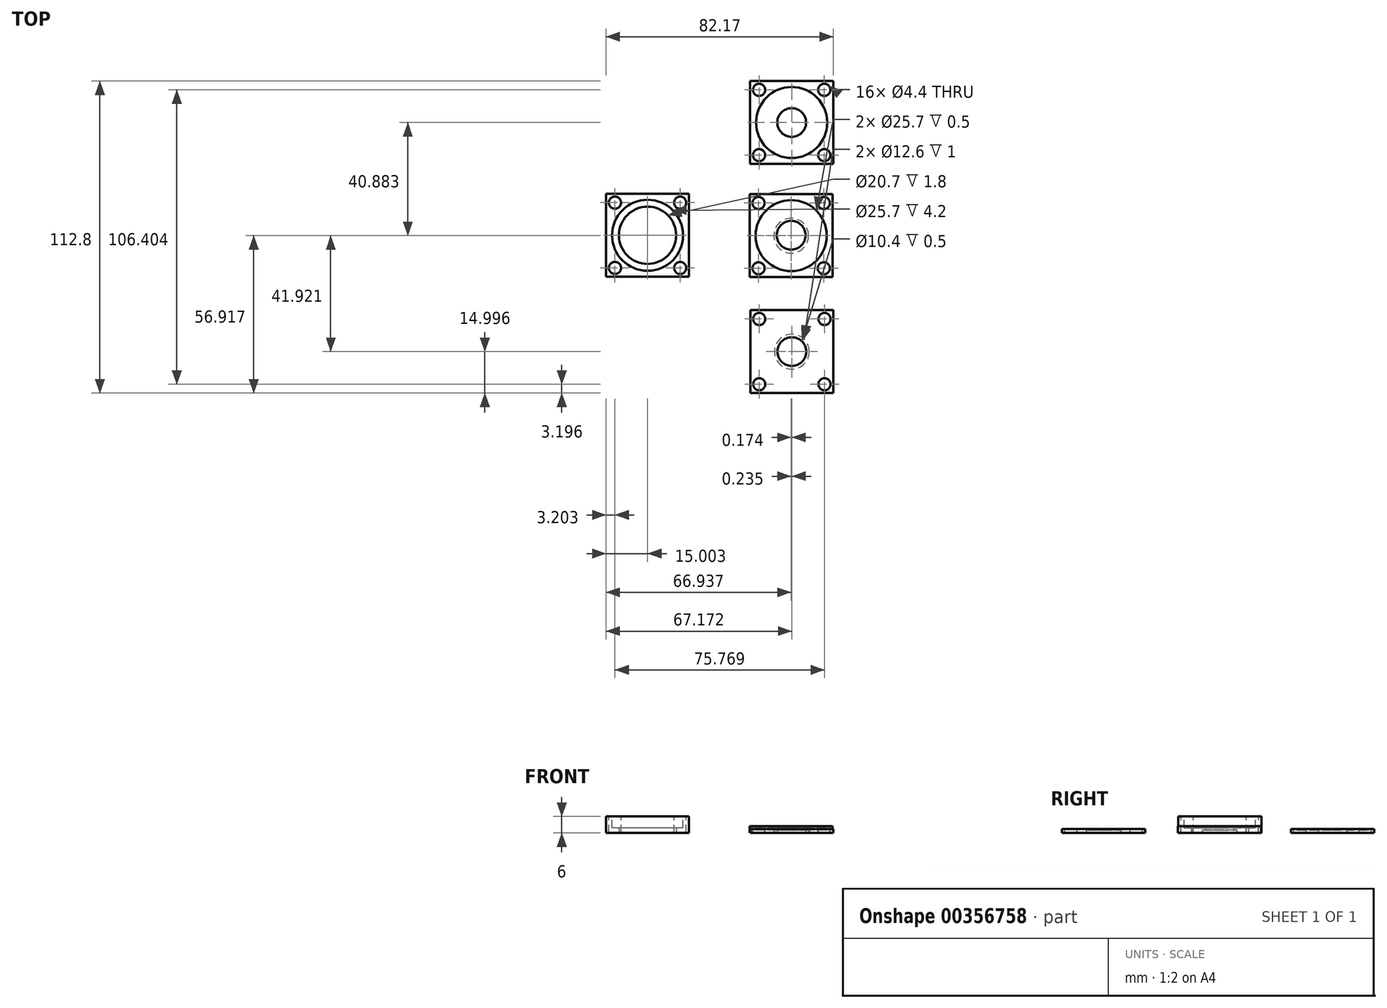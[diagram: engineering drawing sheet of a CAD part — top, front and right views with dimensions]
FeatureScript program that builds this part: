
annotation { "Feature Type Name" : "Feature", "Feature Type Description" : "" }
export const myFeature = defineFeature(function(context is Context, id is Id, definition is map)
    precondition{}
    {
        {
            var Q0;
            Q0=qCreatedBy(makeId("Top.planeOp"),FACE);
            var sketch = newSketch(context, id + "F0", { "sketchPlane" : qUnion([Q0])});
            skLineSegment(sketch, "E0.bottom", {"start": v(-9.76, 15) * mm, "end": v(-39.76, 15) * mm});
            skLineSegment(sketch, "E0.top", {"start": v(-9.76, -15) * mm, "end": v(-39.76, -15) * mm});
            skLineSegment(sketch, "E0.left", {"start": v(-9.76, 15) * mm, "end": v(-9.76, -15) * mm});
            skLineSegment(sketch, "E0.right", {"start": v(-39.76, 15) * mm, "end": v(-39.76, -15) * mm});
            skPoint(sketch, "E0.middle", {"position": v(-24.76, 0) * mm});
            skCircle(sketch, "E1", {"center": v(-24.76, 0) * mm, "radius": 10.35 * mm});
            skSolve(sketch);
        }
        {
            var Q0;
            Q0=makeQuery(id+"F0.imprint","IMPRINT",FACE,{"disambiguationData":[TD([[makeQuery(id+"F0.imprint","IMPRINT",EDGE,{"derivedFrom":sQuery(id+"F0.wireOp",EDGE,"E0.bottom")}),1.0]])]});
            extrude(context, id + "F1", {"entities" : qUnion([Q0]), "depth" : 6 * mm});
        }
        {
            var Q0;
            Q0=makeQuery(id+"F1.opExtrude","CAP_FACE",FACE,{"disambiguationData":[OSD([sQuery(id+"F0.wireOp",EDGE,"E0.bottom"),sQuery(id+"F0.wireOp",EDGE,"E0.top"),sQuery(id+"F0.wireOp",EDGE,"E0.left"),sQuery(id+"F0.wireOp",EDGE,"E0.right"),sQuery(id+"F0.wireOp",EDGE,"E1")])],"isStart":false});
            var sketch = newSketch(context, id + "F2", { "sketchPlane" : qUnion([Q0])});
            skLineSegment(sketch, "E2", {"start": v(-24.76, 15) * mm, "end": v(-24.76, -15) * mm, "construction": true});
            skLineSegment(sketch, "E3", {"start": v(-39.76, 0) * mm, "end": v(-9.76, 0) * mm, "construction": true});
            skCircle(sketch, "E4", {"center": v(-24.76, 0) * mm, "radius": 12.85 * mm});
            skSolve(sketch);
        }
        {
            var Q0;
            Q0=makeQuery(id+"F2.imprint","IMPRINT",FACE,{"disambiguationData":[TD([[makeQuery(id+"F2.imprint","IMPRINT",EDGE,{"derivedFrom":sQuery(id+"F2.wireOp",EDGE,"E4")}),1.0]])]});
            extrude(context, id + "F3", {"entities" : qUnion([Q0]), "operationType" : NewBodyOperationType.REMOVE, "oppositeDirection" : true, "depth" : 4.2 * mm});
        }
        {
            var Q0;
            Q0=makeQuery(id+"F1.opExtrude","CAP_FACE",FACE,{"disambiguationData":[OSD([sQuery(id+"F0.wireOp",EDGE,"E0.bottom"),sQuery(id+"F0.wireOp",EDGE,"E0.top"),sQuery(id+"F0.wireOp",EDGE,"E0.left"),sQuery(id+"F0.wireOp",EDGE,"E0.right"),sQuery(id+"F0.wireOp",EDGE,"E1")])],"isStart":false});
            var sketch = newSketch(context, id + "F4", { "sketchPlane" : qUnion([Q0])});
            skLineSegment(sketch, "E5", {"start": v(-24.76, 15) * mm, "end": v(-24.76, -15) * mm, "construction": true});
            skLineSegment(sketch, "E6", {"start": v(-39.76, 0) * mm, "end": v(-9.76, 0) * mm, "construction": true});
            skPoint(sketch, "E7", {"position": v(-36.56, 11.8) * mm});
            skPoint(sketch, "E8", {"position": v(-12.96, 11.8) * mm});
            skPoint(sketch, "E9", {"position": v(-36.56, -11.8) * mm});
            skPoint(sketch, "E10", {"position": v(-12.96, -11.8) * mm});
            skSolve(sketch);
        }
        {
            var Q0;
            Q0=sQuery(id+"F4.wireOp",VERTEX,"E7");
            var Q1;
            Q1=makeQuery(id+"F1.opExtrude","SWEPT_BODY",BODY,{"disambiguationData":[OSD([sQuery(id+"F0.wireOp",EDGE,"E0.bottom"),sQuery(id+"F0.wireOp",EDGE,"E0.top"),sQuery(id+"F0.wireOp",EDGE,"E0.left"),sQuery(id+"F0.wireOp",EDGE,"E0.right"),sQuery(id+"F0.wireOp",EDGE,"E1")])]});
            hole(context, id + "F5", {"style" : HoleStyle.SIMPLE, "endStyle" : HoleEndStyle.THROUGH, "standardTappedOrClearance" : lookupTablePath({ "standard" : "ISO", "fit" : "Normal", "size" : "M4", "type" : "Clearance" }), "standardBlindInLast" : lookupTablePath({ "fit" : "Standard", "standard" : "ISO", "size" : "M4", "type" : "Clearance" }), "holeDiameter" : 4.4 * mm, "isTappedThrough" : true, "tappedDepth" : 12 * mm, "tapClearance" : 3, "startFromSketch" : true, "locations" : qUnion([Q0]), "scope" : qUnion([Q1])});
        }
        {
            var Q0;
            Q0=sQuery(id+"F4.wireOp",VERTEX,"E8");
            var Q1;
            Q1=makeQuery(id+"F1.opExtrude","SWEPT_BODY",BODY,{"disambiguationData":[OSD([sQuery(id+"F0.wireOp",EDGE,"E0.bottom"),sQuery(id+"F0.wireOp",EDGE,"E0.top"),sQuery(id+"F0.wireOp",EDGE,"E0.left"),sQuery(id+"F0.wireOp",EDGE,"E0.right"),sQuery(id+"F0.wireOp",EDGE,"E1")])]});
            hole(context, id + "F6", {"style" : HoleStyle.SIMPLE, "endStyle" : HoleEndStyle.THROUGH, "standardTappedOrClearance" : lookupTablePath({ "standard" : "ISO", "fit" : "Normal", "size" : "M4", "type" : "Clearance" }), "standardBlindInLast" : lookupTablePath({ "fit" : "Standard", "standard" : "ISO", "size" : "M4", "type" : "Clearance" }), "holeDiameter" : 4.4 * mm, "isTappedThrough" : true, "tappedDepth" : 12 * mm, "tapClearance" : 3, "startFromSketch" : true, "locations" : qUnion([Q0]), "scope" : qUnion([Q1])});
        }
        {
            var Q0;
            Q0=sQuery(id+"F4.wireOp",VERTEX,"E9");
            var Q1;
            Q1=makeQuery(id+"F1.opExtrude","SWEPT_BODY",BODY,{"disambiguationData":[OSD([sQuery(id+"F0.wireOp",EDGE,"E0.bottom"),sQuery(id+"F0.wireOp",EDGE,"E0.top"),sQuery(id+"F0.wireOp",EDGE,"E0.left"),sQuery(id+"F0.wireOp",EDGE,"E0.right"),sQuery(id+"F0.wireOp",EDGE,"E1")])]});
            hole(context, id + "F7", {"style" : HoleStyle.SIMPLE, "endStyle" : HoleEndStyle.THROUGH, "standardTappedOrClearance" : lookupTablePath({ "standard" : "ISO", "fit" : "Normal", "size" : "M4", "type" : "Clearance" }), "standardBlindInLast" : lookupTablePath({ "fit" : "Standard", "standard" : "ISO", "size" : "M4", "type" : "Clearance" }), "holeDiameter" : 4.4 * mm, "isTappedThrough" : true, "tappedDepth" : 12 * mm, "tapClearance" : 3, "startFromSketch" : true, "locations" : qUnion([Q0]), "scope" : qUnion([Q1])});
        }
        {
            var Q0;
            Q0=sQuery(id+"F4.wireOp",VERTEX,"E10");
            var Q1;
            Q1=makeQuery(id+"F1.opExtrude","SWEPT_BODY",BODY,{"disambiguationData":[OSD([sQuery(id+"F0.wireOp",EDGE,"E0.bottom"),sQuery(id+"F0.wireOp",EDGE,"E0.top"),sQuery(id+"F0.wireOp",EDGE,"E0.left"),sQuery(id+"F0.wireOp",EDGE,"E0.right"),sQuery(id+"F0.wireOp",EDGE,"E1")])]});
            hole(context, id + "F8", {"style" : HoleStyle.SIMPLE, "endStyle" : HoleEndStyle.THROUGH, "standardTappedOrClearance" : lookupTablePath({ "standard" : "ISO", "fit" : "Normal", "size" : "M4", "type" : "Clearance" }), "standardBlindInLast" : lookupTablePath({ "fit" : "Standard", "standard" : "ISO", "size" : "M4", "type" : "Clearance" }), "holeDiameter" : 4.4 * mm, "isTappedThrough" : true, "tappedDepth" : 12 * mm, "tapClearance" : 3, "startFromSketch" : true, "locations" : qUnion([Q0]), "scope" : qUnion([Q1])});
        }
        {
            var Q0;
            Q0=qCreatedBy(makeId("Top.planeOp"),FACE);
            var sketch = newSketch(context, id + "F9", { "sketchPlane" : qUnion([Q0])});
            skLineSegment(sketch, "E11.bottom", {"start": v(12.18, 14.88) * mm, "end": v(42.18, 14.88) * mm});
            skLineSegment(sketch, "E11.top", {"start": v(12.18, -15.12) * mm, "end": v(42.18, -15.12) * mm});
            skLineSegment(sketch, "E11.left", {"start": v(12.18, 14.88) * mm, "end": v(12.18, -15.12) * mm});
            skLineSegment(sketch, "E11.right", {"start": v(42.18, 14.88) * mm, "end": v(42.18, -15.12) * mm});
            skSolve(sketch);
        }
        {
            var Q0;
            Q0=makeQuery(id+"F9.imprint","IMPRINT",FACE,{"disambiguationData":[TD([[makeQuery(id+"F9.imprint","IMPRINT",EDGE,{"derivedFrom":sQuery(id+"F9.wireOp",EDGE,"E11.bottom")}),-1.0]])]});
            extrude(context, id + "F10", {"entities" : qUnion([Q0]), "depth" : 2.5 * mm});
        }
        {
            var Q0;
            Q0=makeQuery(id+"F10.opExtrude","CAP_FACE",FACE,{"disambiguationData":[OSD([sQuery(id+"F9.wireOp",EDGE,"E11.bottom"),sQuery(id+"F9.wireOp",EDGE,"E11.top"),sQuery(id+"F9.wireOp",EDGE,"E11.left"),sQuery(id+"F9.wireOp",EDGE,"E11.right")])],"isStart":true});
            var sketch = newSketch(context, id + "F11", { "sketchPlane" : qUnion([Q0])});
            skLineSegment(sketch, "E12", {"start": v(27.18, 15.12) * mm, "end": v(27.18, -14.88) * mm, "construction": true});
            skLineSegment(sketch, "E13", {"start": v(12.18, 0) * mm, "end": v(42.18, 0) * mm, "construction": true});
            skCircle(sketch, "E14", {"center": v(27.18, 0) * mm, "radius": 5.2 * mm});
            skSolve(sketch);
        }
        {
            var Q0;
            Q0=makeQuery(id+"F11.imprint","IMPRINT",FACE,{"disambiguationData":[TD([[makeQuery(id+"F11.imprint","IMPRINT",EDGE,{"derivedFrom":sQuery(id+"F11.wireOp",EDGE,"E14")}),1.0]])]});
            extrude(context, id + "F12", {"entities" : qUnion([Q0]), "operationType" : NewBodyOperationType.REMOVE, "endBound" : BoundingType.THROUGH_ALL, "oppositeDirection" : true, "depth" : 2.5 * mm});
        }
        {
            var Q0;
            Q0=makeQuery(id+"F10.opExtrude","CAP_FACE",FACE,{"disambiguationData":[OSD([sQuery(id+"F9.wireOp",EDGE,"E11.bottom"),sQuery(id+"F9.wireOp",EDGE,"E11.top"),sQuery(id+"F9.wireOp",EDGE,"E11.left"),sQuery(id+"F9.wireOp",EDGE,"E11.right")])],"isStart":false});
            var sketch = newSketch(context, id + "F13", { "sketchPlane" : qUnion([Q0])});
            skLineSegment(sketch, "E15", {"start": v(27.18, 14.88) * mm, "end": v(27.18, -15.12) * mm, "construction": true});
            skLineSegment(sketch, "E16", {"start": v(12.18, -0.12) * mm, "end": v(42.18, -0.12) * mm, "construction": true});
            skCircle(sketch, "E17", {"center": v(27.18, -0.12) * mm, "radius": 12.85 * mm});
            skSolve(sketch);
        }
        {
            var Q0;
            Q0=makeQuery(id+"F13.imprint","IMPRINT",FACE,{"disambiguationData":[TD([[makeQuery(id+"F13.imprint","IMPRINT",EDGE,{"derivedFrom":sQuery(id+"F13.wireOp",EDGE,"E17")}),1.0]])]});
            extrude(context, id + "F14", {"entities" : qUnion([Q0]), "operationType" : NewBodyOperationType.REMOVE, "oppositeDirection" : true, "depth" : 0.5 * mm});
        }
        {
            var Q0;
            Q0=makeQuery(id+"F10.opExtrude","CAP_FACE",FACE,{"disambiguationData":[OSD([sQuery(id+"F9.wireOp",EDGE,"E11.bottom"),sQuery(id+"F9.wireOp",EDGE,"E11.top"),sQuery(id+"F9.wireOp",EDGE,"E11.left"),sQuery(id+"F9.wireOp",EDGE,"E11.right")])],"isStart":false});
            var sketch = newSketch(context, id + "F15", { "sketchPlane" : qUnion([Q0])});
            skLineSegment(sketch, "E18", {"start": v(27.18, 14.88) * mm, "end": v(27.18, -15.12) * mm, "construction": true});
            skLineSegment(sketch, "E19", {"start": v(12.18, -0.12) * mm, "end": v(42.18, -0.12) * mm, "construction": true});
            skPoint(sketch, "E20", {"position": v(15.38, 11.68) * mm});
            skPoint(sketch, "E21", {"position": v(38.98, 11.68) * mm});
            skPoint(sketch, "E22", {"position": v(38.98, -11.92) * mm});
            skPoint(sketch, "E23", {"position": v(15.38, -11.92) * mm});
            skSolve(sketch);
        }
        {
            var Q0;
            Q0=sQuery(id+"F15.wireOp",VERTEX,"E20");
            var Q1;
            Q1=makeQuery(id+"F10.opExtrude","SWEPT_BODY",BODY,{"disambiguationData":[OSD([sQuery(id+"F9.wireOp",EDGE,"E11.bottom"),sQuery(id+"F9.wireOp",EDGE,"E11.top"),sQuery(id+"F9.wireOp",EDGE,"E11.left"),sQuery(id+"F9.wireOp",EDGE,"E11.right")])]});
            hole(context, id + "F16", {"style" : HoleStyle.SIMPLE, "endStyle" : HoleEndStyle.THROUGH, "standardTappedOrClearance" : lookupTablePath({ "standard" : "ISO", "fit" : "Normal", "size" : "M4", "type" : "Clearance" }), "standardBlindInLast" : lookupTablePath({ "fit" : "Standard", "standard" : "ISO", "size" : "M4", "type" : "Clearance" }), "holeDiameter" : 4.4 * mm, "isTappedThrough" : true, "tappedDepth" : 12 * mm, "tapClearance" : 3, "startFromSketch" : true, "locations" : qUnion([Q0]), "scope" : qUnion([Q1])});
        }
        {
            var Q0;
            Q0=sQuery(id+"F15.wireOp",VERTEX,"E21");
            var Q1;
            Q1=makeQuery(id+"F10.opExtrude","SWEPT_BODY",BODY,{"disambiguationData":[OSD([sQuery(id+"F9.wireOp",EDGE,"E11.bottom"),sQuery(id+"F9.wireOp",EDGE,"E11.top"),sQuery(id+"F9.wireOp",EDGE,"E11.left"),sQuery(id+"F9.wireOp",EDGE,"E11.right")])]});
            hole(context, id + "F17", {"style" : HoleStyle.SIMPLE, "endStyle" : HoleEndStyle.THROUGH, "standardTappedOrClearance" : lookupTablePath({ "standard" : "ISO", "fit" : "Normal", "size" : "M4", "type" : "Clearance" }), "standardBlindInLast" : lookupTablePath({ "fit" : "Standard", "standard" : "ISO", "size" : "M4", "type" : "Clearance" }), "holeDiameter" : 4.4 * mm, "isTappedThrough" : true, "tappedDepth" : 12 * mm, "tapClearance" : 3, "startFromSketch" : true, "locations" : qUnion([Q0]), "scope" : qUnion([Q1])});
        }
        {
            var Q0;
            Q0=sQuery(id+"F15.wireOp",VERTEX,"E23");
            var Q1;
            Q1=makeQuery(id+"F10.opExtrude","SWEPT_BODY",BODY,{"disambiguationData":[OSD([sQuery(id+"F9.wireOp",EDGE,"E11.bottom"),sQuery(id+"F9.wireOp",EDGE,"E11.top"),sQuery(id+"F9.wireOp",EDGE,"E11.left"),sQuery(id+"F9.wireOp",EDGE,"E11.right")])]});
            hole(context, id + "F18", {"style" : HoleStyle.SIMPLE, "endStyle" : HoleEndStyle.THROUGH, "standardTappedOrClearance" : lookupTablePath({ "standard" : "ISO", "fit" : "Normal", "size" : "M4", "type" : "Clearance" }), "standardBlindInLast" : lookupTablePath({ "fit" : "Standard", "standard" : "ISO", "size" : "M4", "type" : "Clearance" }), "holeDiameter" : 4.4 * mm, "isTappedThrough" : true, "tappedDepth" : 12 * mm, "tapClearance" : 3, "startFromSketch" : true, "locations" : qUnion([Q0]), "scope" : qUnion([Q1])});
        }
        {
            var Q0;
            Q0=sQuery(id+"F15.wireOp",VERTEX,"E22");
            var Q1;
            Q1=makeQuery(id+"F10.opExtrude","SWEPT_BODY",BODY,{"disambiguationData":[OSD([sQuery(id+"F9.wireOp",EDGE,"E11.bottom"),sQuery(id+"F9.wireOp",EDGE,"E11.top"),sQuery(id+"F9.wireOp",EDGE,"E11.left"),sQuery(id+"F9.wireOp",EDGE,"E11.right")])]});
            hole(context, id + "F19", {"style" : HoleStyle.SIMPLE, "endStyle" : HoleEndStyle.THROUGH, "standardTappedOrClearance" : lookupTablePath({ "standard" : "ISO", "fit" : "Normal", "size" : "M4", "type" : "Clearance" }), "standardBlindInLast" : lookupTablePath({ "fit" : "Standard", "standard" : "ISO", "size" : "M4", "type" : "Clearance" }), "holeDiameter" : 4.4 * mm, "isTappedThrough" : true, "tappedDepth" : 12 * mm, "tapClearance" : 3, "startFromSketch" : true, "locations" : qUnion([Q0]), "scope" : qUnion([Q1])});
        }
        {
            var Q0;
            Q0=makeQuery(id+"F10.opExtrude","CAP_FACE",FACE,{"disambiguationData":[OSD([sQuery(id+"F9.wireOp",EDGE,"E11.bottom"),sQuery(id+"F9.wireOp",EDGE,"E11.top"),sQuery(id+"F9.wireOp",EDGE,"E11.left"),sQuery(id+"F9.wireOp",EDGE,"E11.right")])],"isStart":true});
            var sketch = newSketch(context, id + "F20", { "sketchPlane" : qUnion([Q0])});
            skLineSegment(sketch, "E24", {"start": v(12.18, 0.12) * mm, "end": v(42.18, 0.12) * mm, "construction": true});
            skLineSegment(sketch, "E25", {"start": v(27.18, 15.12) * mm, "end": v(27.18, -14.88) * mm, "construction": true});
            skCircle(sketch, "E26", {"center": v(27.18, 0.12) * mm, "radius": 6.3 * mm});
            skSolve(sketch);
        }
        {
            var Q0;
            Q0=makeQuery(id+"F20.imprint","IMPRINT",FACE,{"disambiguationData":[TD([[makeQuery(id+"F20.imprint","IMPRINT",EDGE,{"derivedFrom":sQuery(id+"F20.wireOp",EDGE,"E26")}),1.0]])]});
            extrude(context, id + "F21", {"entities" : qUnion([Q0]), "operationType" : NewBodyOperationType.REMOVE, "oppositeDirection" : true, "depth" : 1 * mm});
        }
        {
            var Q0;
            Q0=qCreatedBy(makeId("Top.planeOp"),FACE);
            var sketch = newSketch(context, id + "F22", { "sketchPlane" : qUnion([Q0])});
            skLineSegment(sketch, "E27.bottom", {"start": v(12.35, 25.76) * mm, "end": v(42.35, 25.76) * mm});
            skLineSegment(sketch, "E27.top", {"start": v(12.35, 55.76) * mm, "end": v(42.35, 55.76) * mm});
            skLineSegment(sketch, "E27.left", {"start": v(12.35, 25.76) * mm, "end": v(12.35, 55.76) * mm});
            skLineSegment(sketch, "E27.right", {"start": v(42.35, 25.76) * mm, "end": v(42.35, 55.76) * mm});
            skSolve(sketch);
        }
        {
            var Q0;
            Q0=makeQuery(id+"F22.imprint","IMPRINT",FACE,{"disambiguationData":[TD([[makeQuery(id+"F22.imprint","IMPRINT",EDGE,{"derivedFrom":sQuery(id+"F22.wireOp",EDGE,"E27.bottom")}),1.0]])]});
            extrude(context, id + "F23", {"entities" : qUnion([Q0]), "depth" : 1.5 * mm});
        }
        {
            var Q0;
            Q0=makeQuery(id+"F23.opExtrude","CAP_FACE",FACE,{"disambiguationData":[OSD([sQuery(id+"F22.wireOp",EDGE,"E27.bottom"),sQuery(id+"F22.wireOp",EDGE,"E27.top"),sQuery(id+"F22.wireOp",EDGE,"E27.left"),sQuery(id+"F22.wireOp",EDGE,"E27.right")])],"isStart":false});
            var sketch = newSketch(context, id + "F24", { "sketchPlane" : qUnion([Q0])});
            skLineSegment(sketch, "E28", {"start": v(12.35, 40.76) * mm, "end": v(42.35, 40.76) * mm, "construction": true});
            skLineSegment(sketch, "E29", {"start": v(27.35, 55.76) * mm, "end": v(27.35, 25.76) * mm, "construction": true});
            skCircle(sketch, "E30", {"center": v(27.35, 40.76) * mm, "radius": 12.85 * mm});
            skSolve(sketch);
        }
        {
            var Q0;
            Q0 = qSketchRegion(id + "F24", true);
            extrude(context, id + "F25", {"entities" : qUnion([Q0]), "operationType" : NewBodyOperationType.REMOVE, "oppositeDirection" : true, "depth" : 0.5 * mm});
        }
        {
            var Q0;
            Q0=makeQuery(id+"F23.opExtrude","CAP_FACE",FACE,{"disambiguationData":[OSD([sQuery(id+"F22.wireOp",EDGE,"E27.bottom"),sQuery(id+"F22.wireOp",EDGE,"E27.top"),sQuery(id+"F22.wireOp",EDGE,"E27.left"),sQuery(id+"F22.wireOp",EDGE,"E27.right")])],"isStart":true});
            var sketch = newSketch(context, id + "F26", { "sketchPlane" : qUnion([Q0])});
            skLineSegment(sketch, "E31", {"start": v(27.35, -25.76) * mm, "end": v(27.35, -55.76) * mm, "construction": true});
            skLineSegment(sketch, "E32", {"start": v(12.35, -40.76) * mm, "end": v(42.35, -40.76) * mm, "construction": true});
            skCircle(sketch, "E33", {"center": v(27.35, -40.76) * mm, "radius": 5.2 * mm});
            skSolve(sketch);
        }
        {
            var Q0;
            Q0=makeQuery(id+"F26.imprint","IMPRINT",FACE,{"disambiguationData":[TD([[makeQuery(id+"F26.imprint","IMPRINT",EDGE,{"derivedFrom":sQuery(id+"F26.wireOp",EDGE,"E33")}),1.0]])]});
            extrude(context, id + "F27", {"entities" : qUnion([Q0]), "operationType" : NewBodyOperationType.REMOVE, "endBound" : BoundingType.THROUGH_ALL, "oppositeDirection" : true, "depth" : 25 * mm});
        }
        {
            var Q0;
            Q0=makeQuery(id+"F23.opExtrude","CAP_FACE",FACE,{"disambiguationData":[OSD([sQuery(id+"F22.wireOp",EDGE,"E27.bottom"),sQuery(id+"F22.wireOp",EDGE,"E27.top"),sQuery(id+"F22.wireOp",EDGE,"E27.left"),sQuery(id+"F22.wireOp",EDGE,"E27.right")])],"isStart":false});
            var sketch = newSketch(context, id + "F28", { "sketchPlane" : qUnion([Q0])});
            skLineSegment(sketch, "E34", {"start": v(27.35, 55.76) * mm, "end": v(27.35, 25.76) * mm, "construction": true});
            skLineSegment(sketch, "E35", {"start": v(12.35, 40.76) * mm, "end": v(42.35, 40.76) * mm, "construction": true});
            skPoint(sketch, "E36", {"position": v(15.55, 52.56) * mm});
            skPoint(sketch, "E37", {"position": v(39.15, 52.56) * mm});
            skPoint(sketch, "E38", {"position": v(39.15, 28.96) * mm});
            skPoint(sketch, "E39", {"position": v(15.55, 28.96) * mm});
            skPoint(sketch, "E40", {"position": v(-10.13, 45.95) * mm});
            skSolve(sketch);
        }
        {
            var Q0;
            Q0=sQuery(id+"F28.wireOp",VERTEX,"E36");
            var Q1;
            Q1=makeQuery(id+"F23.opExtrude","SWEPT_BODY",BODY,{"disambiguationData":[OSD([sQuery(id+"F22.wireOp",EDGE,"E27.bottom"),sQuery(id+"F22.wireOp",EDGE,"E27.top"),sQuery(id+"F22.wireOp",EDGE,"E27.left"),sQuery(id+"F22.wireOp",EDGE,"E27.right")])]});
            hole(context, id + "F29", {"style" : HoleStyle.SIMPLE, "endStyle" : HoleEndStyle.THROUGH, "standardTappedOrClearance" : lookupTablePath({ "standard" : "ISO", "fit" : "Normal", "size" : "M4", "type" : "Clearance" }), "standardBlindInLast" : lookupTablePath({ "fit" : "Standard", "standard" : "ISO", "size" : "M4", "type" : "Clearance" }), "holeDiameter" : 4.4 * mm, "isTappedThrough" : true, "tappedDepth" : 12 * mm, "tapClearance" : 3, "startFromSketch" : true, "locations" : qUnion([Q0]), "scope" : qUnion([Q1])});
        }
        {
            var Q0;
            Q0=sQuery(id+"F28.wireOp",VERTEX,"E37");
            var Q1;
            Q1=makeQuery(id+"F23.opExtrude","SWEPT_BODY",BODY,{"disambiguationData":[OSD([sQuery(id+"F22.wireOp",EDGE,"E27.bottom"),sQuery(id+"F22.wireOp",EDGE,"E27.top"),sQuery(id+"F22.wireOp",EDGE,"E27.left"),sQuery(id+"F22.wireOp",EDGE,"E27.right")])]});
            hole(context, id + "F30", {"style" : HoleStyle.SIMPLE, "endStyle" : HoleEndStyle.THROUGH, "standardTappedOrClearance" : lookupTablePath({ "standard" : "ISO", "fit" : "Normal", "size" : "M4", "type" : "Clearance" }), "standardBlindInLast" : lookupTablePath({ "fit" : "Standard", "standard" : "ISO", "size" : "M4", "type" : "Clearance" }), "holeDiameter" : 4.4 * mm, "isTappedThrough" : true, "tappedDepth" : 12 * mm, "tapClearance" : 3, "startFromSketch" : true, "locations" : qUnion([Q0]), "scope" : qUnion([Q1])});
        }
        {
            var Q0;
            Q0=sQuery(id+"F28.wireOp",VERTEX,"E39");
            var Q1;
            Q1=makeQuery(id+"F23.opExtrude","SWEPT_BODY",BODY,{"disambiguationData":[OSD([sQuery(id+"F22.wireOp",EDGE,"E27.bottom"),sQuery(id+"F22.wireOp",EDGE,"E27.top"),sQuery(id+"F22.wireOp",EDGE,"E27.left"),sQuery(id+"F22.wireOp",EDGE,"E27.right")])]});
            hole(context, id + "F31", {"style" : HoleStyle.SIMPLE, "endStyle" : HoleEndStyle.THROUGH, "standardTappedOrClearance" : lookupTablePath({ "standard" : "ISO", "fit" : "Normal", "size" : "M4", "type" : "Clearance" }), "standardBlindInLast" : lookupTablePath({ "fit" : "Standard", "standard" : "ISO", "size" : "M4", "type" : "Clearance" }), "holeDiameter" : 4.4 * mm, "isTappedThrough" : true, "tappedDepth" : 12 * mm, "tapClearance" : 3, "startFromSketch" : true, "locations" : qUnion([Q0]), "scope" : qUnion([Q1])});
        }
        {
            var Q0;
            Q0=sQuery(id+"F28.wireOp",VERTEX,"E38");
            var Q1;
            Q1=makeQuery(id+"F23.opExtrude","SWEPT_BODY",BODY,{"disambiguationData":[OSD([sQuery(id+"F22.wireOp",EDGE,"E27.bottom"),sQuery(id+"F22.wireOp",EDGE,"E27.top"),sQuery(id+"F22.wireOp",EDGE,"E27.left"),sQuery(id+"F22.wireOp",EDGE,"E27.right")])]});
            hole(context, id + "F32", {"style" : HoleStyle.SIMPLE, "endStyle" : HoleEndStyle.THROUGH, "standardTappedOrClearance" : lookupTablePath({ "standard" : "ISO", "fit" : "Normal", "size" : "M4", "type" : "Clearance" }), "standardBlindInLast" : lookupTablePath({ "fit" : "Standard", "standard" : "ISO", "size" : "M4", "type" : "Clearance" }), "holeDiameter" : 4.4 * mm, "isTappedThrough" : true, "tappedDepth" : 12 * mm, "tapClearance" : 3, "startFromSketch" : true, "locations" : qUnion([Q0]), "scope" : qUnion([Q1])});
        }
        {
            var Q0;
            Q0=qCreatedBy(makeId("Top.planeOp"),FACE);
            var sketch = newSketch(context, id + "F33", { "sketchPlane" : qUnion([Q0])});
            skLineSegment(sketch, "E41.bottom", {"start": v(12.41, -57.04) * mm, "end": v(42.41, -57.04) * mm});
            skLineSegment(sketch, "E41.top", {"start": v(12.41, -27.04) * mm, "end": v(42.41, -27.04) * mm});
            skLineSegment(sketch, "E41.left", {"start": v(12.41, -57.04) * mm, "end": v(12.41, -27.04) * mm});
            skLineSegment(sketch, "E41.right", {"start": v(42.41, -57.04) * mm, "end": v(42.41, -27.04) * mm});
            skSolve(sketch);
        }
        {
            var Q0;
            Q0 = qSketchRegion(id + "F33", true);
            extrude(context, id + "F34", {"entities" : qUnion([Q0]), "depth" : 1.5 * mm});
        }
        {
            var Q0;
            Q0=makeQuery(id+"F34.opExtrude","CAP_FACE",FACE,{"disambiguationData":[OSD([sQuery(id+"F33.wireOp",EDGE,"E41.bottom"),sQuery(id+"F33.wireOp",EDGE,"E41.top"),sQuery(id+"F33.wireOp",EDGE,"E41.left"),sQuery(id+"F33.wireOp",EDGE,"E41.right")])],"isStart":false});
            var sketch = newSketch(context, id + "F35", { "sketchPlane" : qUnion([Q0])});
            skLineSegment(sketch, "E42", {"start": v(12.41, -42.04) * mm, "end": v(42.41, -42.04) * mm, "construction": true});
            skLineSegment(sketch, "E43", {"start": v(27.41, -57.04) * mm, "end": v(27.41, -27.04) * mm, "construction": true});
            skCircle(sketch, "E44", {"center": v(27.41, -42.04) * mm, "radius": 5.2 * mm});
            skSolve(sketch);
        }
        {
            var Q0;
            Q0=makeQuery(id+"F35.imprint","IMPRINT",FACE,{"disambiguationData":[TD([[makeQuery(id+"F35.imprint","IMPRINT",EDGE,{"derivedFrom":sQuery(id+"F35.wireOp",EDGE,"E44")}),1.0]])]});
            extrude(context, id + "F36", {"entities" : qUnion([Q0]), "operationType" : NewBodyOperationType.REMOVE, "oppositeDirection" : true, "depth" : 1.5 * mm});
        }
        {
            var Q0;
            Q0=makeQuery(id+"F34.opExtrude","CAP_FACE",FACE,{"disambiguationData":[OSD([sQuery(id+"F33.wireOp",EDGE,"E41.bottom"),sQuery(id+"F33.wireOp",EDGE,"E41.top"),sQuery(id+"F33.wireOp",EDGE,"E41.left"),sQuery(id+"F33.wireOp",EDGE,"E41.right")])],"isStart":true});
            var sketch = newSketch(context, id + "F37", { "sketchPlane" : qUnion([Q0])});
            skLineSegment(sketch, "E45", {"start": v(42.41, 42.04) * mm, "end": v(12.41, 42.04) * mm, "construction": true});
            skLineSegment(sketch, "E46", {"start": v(27.41, 57.04) * mm, "end": v(27.41, 27.04) * mm, "construction": true});
            skCircle(sketch, "E47", {"center": v(27.41, 42.04) * mm, "radius": 6.3 * mm});
            skSolve(sketch);
        }
        {
            var Q0;
            Q0=makeQuery(id+"F37.imprint","IMPRINT",FACE,{"disambiguationData":[TD([[makeQuery(id+"F37.imprint","IMPRINT",EDGE,{"derivedFrom":sQuery(id+"F37.wireOp",EDGE,"E47")}),1.0]])]});
            extrude(context, id + "F38", {"entities" : qUnion([Q0]), "operationType" : NewBodyOperationType.REMOVE, "oppositeDirection" : true, "depth" : 1 * mm});
        }
        {
            var Q0;
            Q0=makeQuery(id+"F34.opExtrude","CAP_FACE",FACE,{"disambiguationData":[OSD([sQuery(id+"F33.wireOp",EDGE,"E41.bottom"),sQuery(id+"F33.wireOp",EDGE,"E41.top"),sQuery(id+"F33.wireOp",EDGE,"E41.left"),sQuery(id+"F33.wireOp",EDGE,"E41.right")])],"isStart":false});
            var sketch = newSketch(context, id + "F39", { "sketchPlane" : qUnion([Q0])});
            skLineSegment(sketch, "E48", {"start": v(12.41, -42.04) * mm, "end": v(42.41, -42.04) * mm, "construction": true});
            skLineSegment(sketch, "E49", {"start": v(27.41, -57.04) * mm, "end": v(27.41, -27.04) * mm, "construction": true});
            skPoint(sketch, "E50", {"position": v(15.61, -53.84) * mm});
            skPoint(sketch, "E51", {"position": v(15.61, -30.24) * mm});
            skPoint(sketch, "E52", {"position": v(39.21, -30.24) * mm});
            skPoint(sketch, "E53", {"position": v(39.21, -53.84) * mm});
            skSolve(sketch);
        }
        {
            var Q0;
            Q0=sQuery(id+"F39.wireOp",VERTEX,"E50");
            var Q1;
            Q1=makeQuery(id+"F34.opExtrude","SWEPT_BODY",BODY,{"disambiguationData":[OSD([sQuery(id+"F33.wireOp",EDGE,"E41.bottom"),sQuery(id+"F33.wireOp",EDGE,"E41.top"),sQuery(id+"F33.wireOp",EDGE,"E41.left"),sQuery(id+"F33.wireOp",EDGE,"E41.right")])]});
            hole(context, id + "F40", {"style" : HoleStyle.SIMPLE, "endStyle" : HoleEndStyle.THROUGH, "standardTappedOrClearance" : lookupTablePath({ "standard" : "ISO", "fit" : "Normal", "size" : "M4", "type" : "Clearance" }), "standardBlindInLast" : lookupTablePath({ "fit" : "Standard", "standard" : "ISO", "size" : "M4", "type" : "Clearance" }), "holeDiameter" : 4.4 * mm, "isTappedThrough" : true, "tappedDepth" : 12 * mm, "tapClearance" : 3, "startFromSketch" : true, "locations" : qUnion([Q0]), "scope" : qUnion([Q1])});
        }
        {
            var Q0;
            Q0=sQuery(id+"F39.wireOp",VERTEX,"E51");
            var Q1;
            Q1=makeQuery(id+"F34.opExtrude","SWEPT_BODY",BODY,{"disambiguationData":[OSD([sQuery(id+"F33.wireOp",EDGE,"E41.bottom"),sQuery(id+"F33.wireOp",EDGE,"E41.top"),sQuery(id+"F33.wireOp",EDGE,"E41.left"),sQuery(id+"F33.wireOp",EDGE,"E41.right")])]});
            hole(context, id + "F41", {"style" : HoleStyle.SIMPLE, "endStyle" : HoleEndStyle.THROUGH, "standardTappedOrClearance" : lookupTablePath({ "standard" : "ISO", "fit" : "Normal", "size" : "M4", "type" : "Clearance" }), "standardBlindInLast" : lookupTablePath({ "fit" : "Standard", "standard" : "ISO", "size" : "M4", "type" : "Clearance" }), "holeDiameter" : 4.4 * mm, "isTappedThrough" : true, "tappedDepth" : 12 * mm, "tapClearance" : 3, "startFromSketch" : true, "locations" : qUnion([Q0]), "scope" : qUnion([Q1])});
        }
        {
            var Q0;
            Q0=sQuery(id+"F39.wireOp",VERTEX,"E53");
            var Q1;
            Q1=makeQuery(id+"F34.opExtrude","SWEPT_BODY",BODY,{"disambiguationData":[OSD([sQuery(id+"F33.wireOp",EDGE,"E41.bottom"),sQuery(id+"F33.wireOp",EDGE,"E41.top"),sQuery(id+"F33.wireOp",EDGE,"E41.left"),sQuery(id+"F33.wireOp",EDGE,"E41.right")])]});
            hole(context, id + "F42", {"style" : HoleStyle.SIMPLE, "endStyle" : HoleEndStyle.THROUGH, "standardTappedOrClearance" : lookupTablePath({ "standard" : "ISO", "fit" : "Normal", "size" : "M4", "type" : "Clearance" }), "standardBlindInLast" : lookupTablePath({ "fit" : "Standard", "standard" : "ISO", "size" : "M4", "type" : "Clearance" }), "holeDiameter" : 4.4 * mm, "isTappedThrough" : true, "tappedDepth" : 12 * mm, "tapClearance" : 3, "startFromSketch" : true, "locations" : qUnion([Q0]), "scope" : qUnion([Q1])});
        }
        {
            var Q0;
            Q0=sQuery(id+"F39.wireOp",VERTEX,"E52");
            var Q1;
            Q1=makeQuery(id+"F34.opExtrude","SWEPT_BODY",BODY,{"disambiguationData":[OSD([sQuery(id+"F33.wireOp",EDGE,"E41.bottom"),sQuery(id+"F33.wireOp",EDGE,"E41.top"),sQuery(id+"F33.wireOp",EDGE,"E41.left"),sQuery(id+"F33.wireOp",EDGE,"E41.right")])]});
            hole(context, id + "F43", {"style" : HoleStyle.SIMPLE, "endStyle" : HoleEndStyle.THROUGH, "standardTappedOrClearance" : lookupTablePath({ "standard" : "ISO", "fit" : "Normal", "size" : "M4", "type" : "Clearance" }), "standardBlindInLast" : lookupTablePath({ "fit" : "Standard", "standard" : "ISO", "size" : "M4", "type" : "Clearance" }), "holeDiameter" : 4.4 * mm, "isTappedThrough" : true, "tappedDepth" : 12 * mm, "tapClearance" : 3, "startFromSketch" : true, "locations" : qUnion([Q0]), "scope" : qUnion([Q1])});
        }
    });
